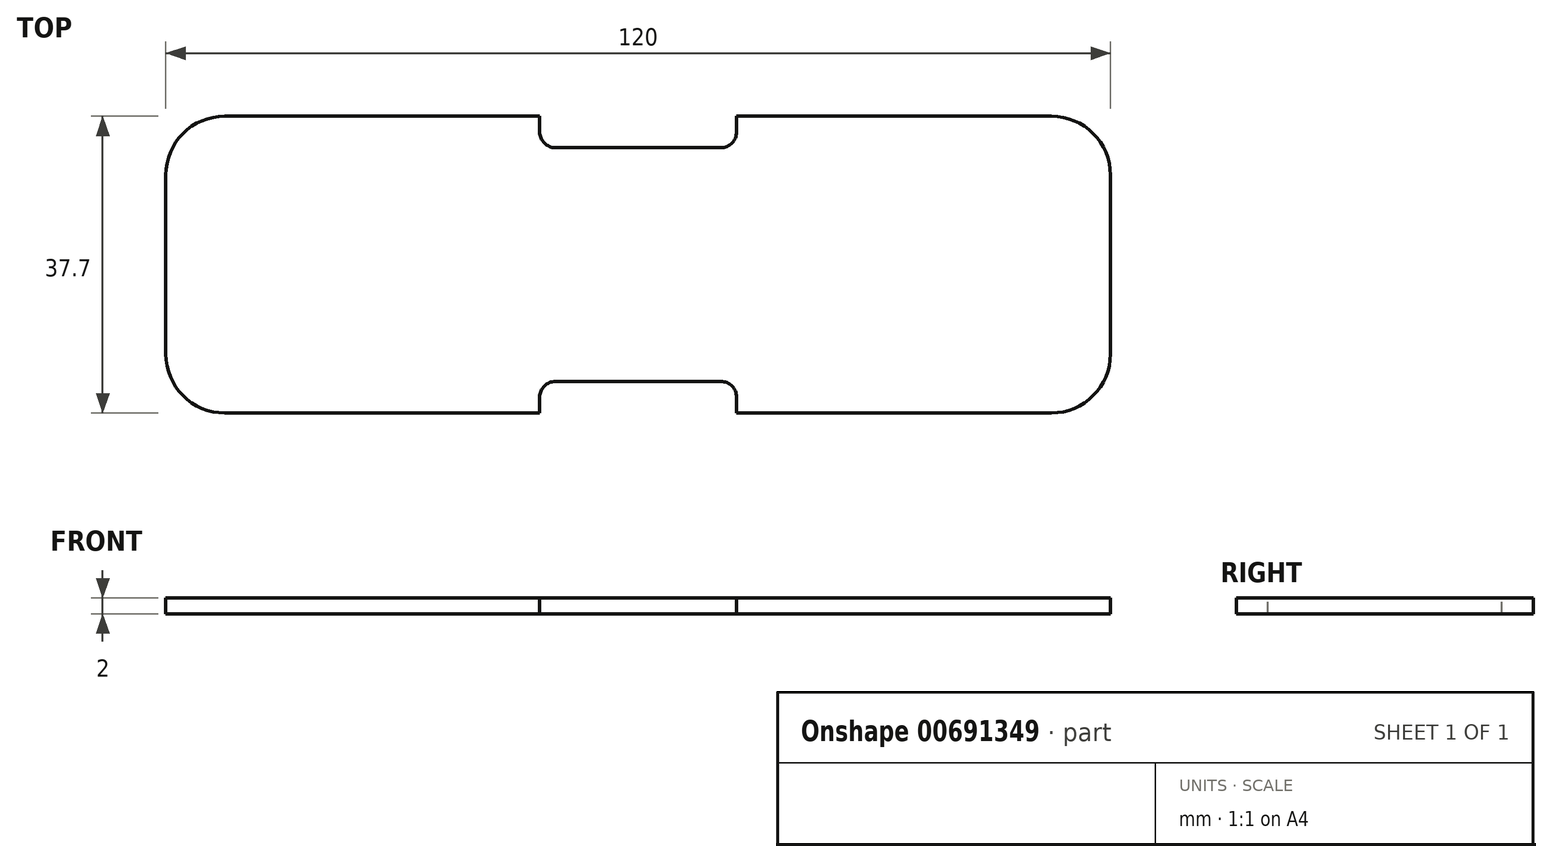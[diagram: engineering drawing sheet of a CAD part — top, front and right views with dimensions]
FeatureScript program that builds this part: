
annotation { "Feature Type Name" : "Feature", "Feature Type Description" : "" }
export const myFeature = defineFeature(function(context is Context, id is Id, definition is map)
    precondition{}
    {
        {
            var Q0;
            Q0=qCreatedBy(makeId("Top.planeOp"),FACE);
            var sketch = newSketch(context, id + "F0", { "sketchPlane" : qUnion([Q0])});
            skLineSegment(sketch, "E0.bottom", {"start": v(60, 18.85) * mm, "end": v(-60, 18.85) * mm});
            skLineSegment(sketch, "E0.top", {"start": v(60, -18.85) * mm, "end": v(-60, -18.85) * mm});
            skLineSegment(sketch, "E0.left", {"start": v(60, 18.85) * mm, "end": v(60, -18.85) * mm});
            skLineSegment(sketch, "E0.right", {"start": v(-60, 18.85) * mm, "end": v(-60, -18.85) * mm});
            skPoint(sketch, "E0.middle", {"position": v(0, 0) * mm});
            skSolve(sketch);
        }
        {
            var Q0;
            Q0=makeQuery(id+"F0.imprint","IMPRINT",FACE,{"disambiguationData":[TD([[makeQuery(id+"F0.imprint","IMPRINT",EDGE,{"derivedFrom":sQuery(id+"F0.wireOp",EDGE,"E0.bottom")}),1.0]])]});
            extrude(context, id + "F1", {"entities" : qUnion([Q0]), "depth" : 2 * mm, "offsetDistance" : 25 * mm});
        }
        {
            var Q0;
            Q0=makeQuery(id+"F1.opExtrude","CAP_FACE",FACE,{"disambiguationData":[OSD([sQuery(id+"F0.wireOp",EDGE,"E0.bottom"),sQuery(id+"F0.wireOp",EDGE,"E0.top"),sQuery(id+"F0.wireOp",EDGE,"E0.left"),sQuery(id+"F0.wireOp",EDGE,"E0.right")])],"isStart":false});
            var sketch = newSketch(context, id + "F2", { "sketchPlane" : qUnion([Q0])});
            skLineSegment(sketch, "E1.bottom", {"start": v(12.5, 22.85) * mm, "end": v(-12.5, 22.85) * mm});
            skLineSegment(sketch, "E1.top", {"start": v(12.5, 14.85) * mm, "end": v(-12.5, 14.85) * mm});
            skLineSegment(sketch, "E1.left", {"start": v(12.5, 22.85) * mm, "end": v(12.5, 14.85) * mm});
            skLineSegment(sketch, "E1.right", {"start": v(-12.5, 22.85) * mm, "end": v(-12.5, 14.85) * mm});
            skPoint(sketch, "E1.middle", {"position": v(0, 18.85) * mm});
            skLineSegment(sketch, "E2.MirrorCS", {"start": v(-12.5, -22.85) * mm, "end": v(-12.5, -14.85) * mm});
            skLineSegment(sketch, "E3.MirrorCS", {"start": v(12.5, -22.85) * mm, "end": v(-12.5, -22.85) * mm});
            skLineSegment(sketch, "E4.MirrorCS", {"start": v(12.5, -22.85) * mm, "end": v(12.5, -14.85) * mm});
            skLineSegment(sketch, "E5.MirrorCS", {"start": v(12.5, -14.85) * mm, "end": v(-12.5, -14.85) * mm});
            skSolve(sketch);
        }
        {
            var Q0;
            Q0 = qSketchRegion(id + "F2", true);
            extrude(context, id + "F3", {"entities" : qUnion([Q0]), "operationType" : NewBodyOperationType.REMOVE, "oppositeDirection" : true, "depth" : 25 * mm, "offsetDistance" : 25 * mm});
        }
        {
            var Q0;
            Q0=makeQuery(id+"F1.opExtrude","SWEPT_EDGE",EDGE,{"disambiguationData":[OSD([sQuery(id+"F0.wireOp",EDGE,"E0.top"),sQuery(id+"F0.wireOp",EDGE,"E0.right")])]});
            var Q1;
            Q1=makeQuery(id+"F1.opExtrude","SWEPT_EDGE",EDGE,{"disambiguationData":[OSD([sQuery(id+"F0.wireOp",EDGE,"E0.top"),sQuery(id+"F0.wireOp",EDGE,"E0.left")])]});
            var Q2;
            Q2=makeQuery(id+"F1.opExtrude","SWEPT_EDGE",EDGE,{"disambiguationData":[OSD([sQuery(id+"F0.wireOp",EDGE,"E0.bottom"),sQuery(id+"F0.wireOp",EDGE,"E0.left")])]});
            var Q3;
            Q3=makeQuery(id+"F1.opExtrude","SWEPT_EDGE",EDGE,{"disambiguationData":[OSD([sQuery(id+"F0.wireOp",EDGE,"E0.bottom"),sQuery(id+"F0.wireOp",EDGE,"E0.right")])]});
            fillet(context, id + "F4", {"entities" : qUnion([Q0, Q1, Q2, Q3]), "radius" : 7.5 * mm, "tangentPropagation" : true, "allowEdgeOverflow" : false});
        }
        {
            var Q0;
            Q0=makeQuery(id+"F3.boolean.opBoolean","COPY",EDGE,{"derivedFrom":makeQuery(id+"F3.opExtrude","SWEPT_EDGE",EDGE,{"disambiguationData":[OSD([sQuery(id+"F2.wireOp",EDGE,"E1.top"),sQuery(id+"F2.wireOp",EDGE,"E1.right")])]})});
            var Q1;
            Q1=makeQuery(id+"F3.boolean.opBoolean","COPY",EDGE,{"derivedFrom":makeQuery(id+"F3.opExtrude","SWEPT_EDGE",EDGE,{"disambiguationData":[OSD([sQuery(id+"F2.wireOp",EDGE,"E1.top"),sQuery(id+"F2.wireOp",EDGE,"E1.left")])]})});
            var Q2;
            Q2=makeQuery(id+"F3.boolean.opBoolean","COPY",EDGE,{"derivedFrom":makeQuery(id+"F3.opExtrude","SWEPT_EDGE",EDGE,{"disambiguationData":[OSD([sQuery(id+"F2.wireOp",EDGE,"E2.MirrorCS"),sQuery(id+"F2.wireOp",EDGE,"E5.MirrorCS")])]})});
            var Q3;
            Q3=makeQuery(id+"F3.boolean.opBoolean","COPY",EDGE,{"derivedFrom":makeQuery(id+"F3.opExtrude","SWEPT_EDGE",EDGE,{"disambiguationData":[OSD([sQuery(id+"F2.wireOp",EDGE,"E4.MirrorCS"),sQuery(id+"F2.wireOp",EDGE,"E5.MirrorCS")])]})});
            fillet(context, id + "F5", {"entities" : qUnion([Q0, Q1, Q2, Q3]), "radius" : 2 * mm, "tangentPropagation" : true, "allowEdgeOverflow" : false});
        }
    });
